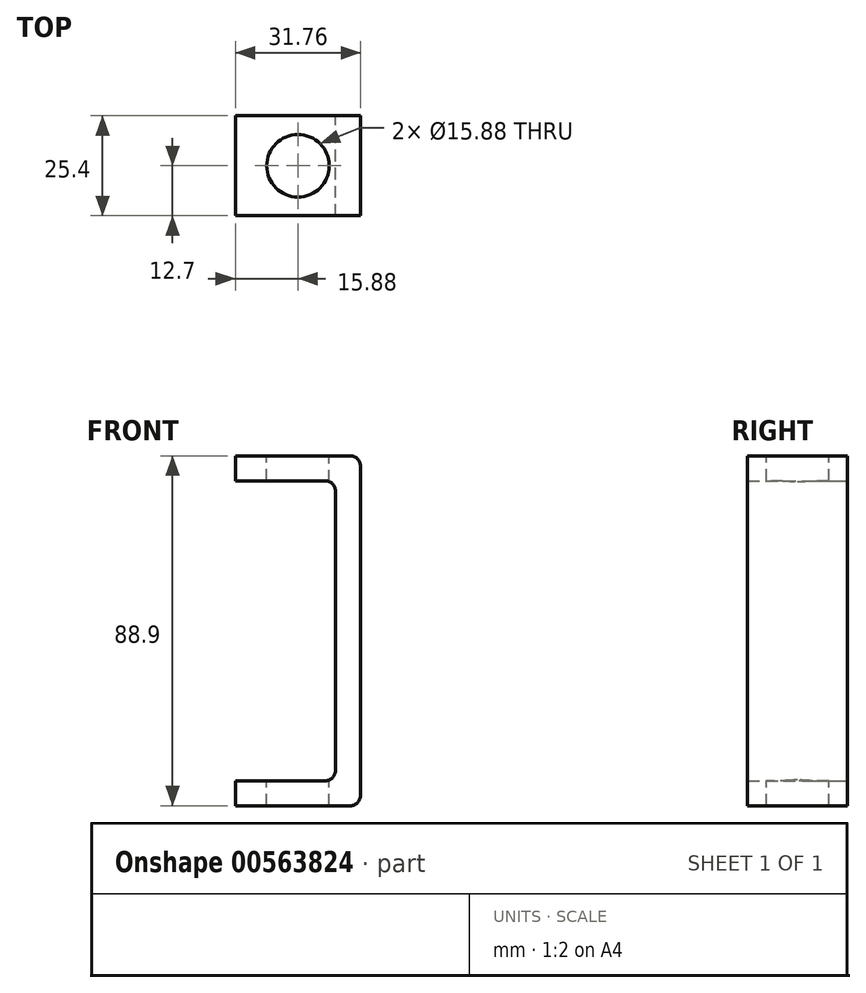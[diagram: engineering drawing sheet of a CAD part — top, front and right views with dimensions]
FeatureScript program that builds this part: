
annotation { "Feature Type Name" : "Feature", "Feature Type Description" : "" }
export const myFeature = defineFeature(function(context is Context, id is Id, definition is map)
    precondition{}
    {
        {
            var Q0;
            Q0=qCreatedBy(makeId("Front.planeOp"),FACE);
            var sketch = newSketch(context, id + "F0", { "sketchPlane" : qUnion([Q0])});
            skLineSegment(sketch, "E0.bottom", {"start": v(-15.87, 44.45) * mm, "end": v(15.88, 44.45) * mm});
            skLineSegment(sketch, "E0.top", {"start": v(-15.88, -44.45) * mm, "end": v(15.87, -44.45) * mm});
            skLineSegment(sketch, "E0.left", {"start": v(-15.87, 44.45) * mm, "end": v(-15.88, -44.45) * mm});
            skLineSegment(sketch, "E0.right", {"start": v(15.88, 44.45) * mm, "end": v(15.87, -44.45) * mm});
            skPoint(sketch, "E0.middle", {"position": v(0, 0) * mm});
            skLineSegment(sketch, "E1", {"start": v(-15.88, -44.45) * mm, "end": v(-15.88, -38.1) * mm});
            skLineSegment(sketch, "E2", {"start": v(-15.88, -38.1) * mm, "end": v(9.52, -38.1) * mm});
            skLineSegment(sketch, "E3", {"start": v(9.52, -38.1) * mm, "end": v(9.52, 38.1) * mm});
            skLineSegment(sketch, "E4", {"start": v(9.52, 38.1) * mm, "end": v(-15.88, 38.1) * mm});
            skSolve(sketch);
        }
        {
            var Q0;
            {var subQ1=sQuery(id+"F0.wireOp",EDGE,"E0.bottom");Q0=makeQuery(id+"F0.imprint","IMPRINT",FACE,{"disambiguationData":[TD([[makeQuery(id+"F0.imprint","IMPRINT",EDGE,{"derivedFrom":subQ1}),-1.0]])]});}
            extrude(context, id + "F1", {"entities" : qUnion([Q0]), "endBound" : BoundingType.SYMMETRIC, "depth" : 25.4 * mm, "offsetDistance" : 25.4 * mm});
        }
        {
            var Q0;
            Q0=makeQuery(id+"F1.opExtrude","SWEPT_EDGE",EDGE,{"disambiguationData":[OSD([sQuery(id+"F0.wireOp",EDGE,"E0.bottom"),sQuery(id+"F0.wireOp",EDGE,"E0.right")])]});
            var Q1;
            Q1=makeQuery(id+"F1.opExtrude","SWEPT_EDGE",EDGE,{"disambiguationData":[OSD([sQuery(id+"F0.wireOp",EDGE,"E0.top"),sQuery(id+"F0.wireOp",EDGE,"E0.right")])]});
            var Q2;
            Q2=makeQuery(id+"F1.opExtrude","SWEPT_EDGE",EDGE,{"disambiguationData":[OSD([sQuery(id+"F0.wireOp",EDGE,"E3"),sQuery(id+"F0.wireOp",EDGE,"E4")])]});
            var Q3;
            Q3=makeQuery(id+"F1.opExtrude","SWEPT_EDGE",EDGE,{"disambiguationData":[OSD([sQuery(id+"F0.wireOp",EDGE,"E2"),sQuery(id+"F0.wireOp",EDGE,"E3")])]});
            fillet(context, id + "F2", {"entities" : qUnion([Q0, Q1, Q2, Q3]), "radius" : 2.54 * mm, "tangentPropagation" : true, "allowEdgeOverflow" : false});
        }
        {
            var Q0;
            Q0=makeQuery(id+"F1.opExtrude","SWEPT_FACE",FACE,{"disambiguationData":[OSD([sQuery(id+"F0.wireOp",EDGE,"E0.bottom")])]});
            var sketch = newSketch(context, id + "F3", { "sketchPlane" : qUnion([Q0])});
            skCircle(sketch, "E5", {"center": v(0, 0) * mm, "radius": 7.94 * mm});
            skSolve(sketch);
        }
        {
            var Q0;
            Q0=makeQuery(id+"F3.imprint","IMPRINT",FACE,{"disambiguationData":[TD([[makeQuery(id+"F3.imprint","IMPRINT",EDGE,{"derivedFrom":sQuery(id+"F3.wireOp",EDGE,"E5")}),1.0]])]});
            extrude(context, id + "F4", {"entities" : qUnion([Q0]), "operationType" : NewBodyOperationType.REMOVE, "endBound" : BoundingType.SYMMETRIC, "oppositeDirection" : true, "depth" : 254 * mm, "offsetDistance" : 25.4 * mm});
        }
    });
